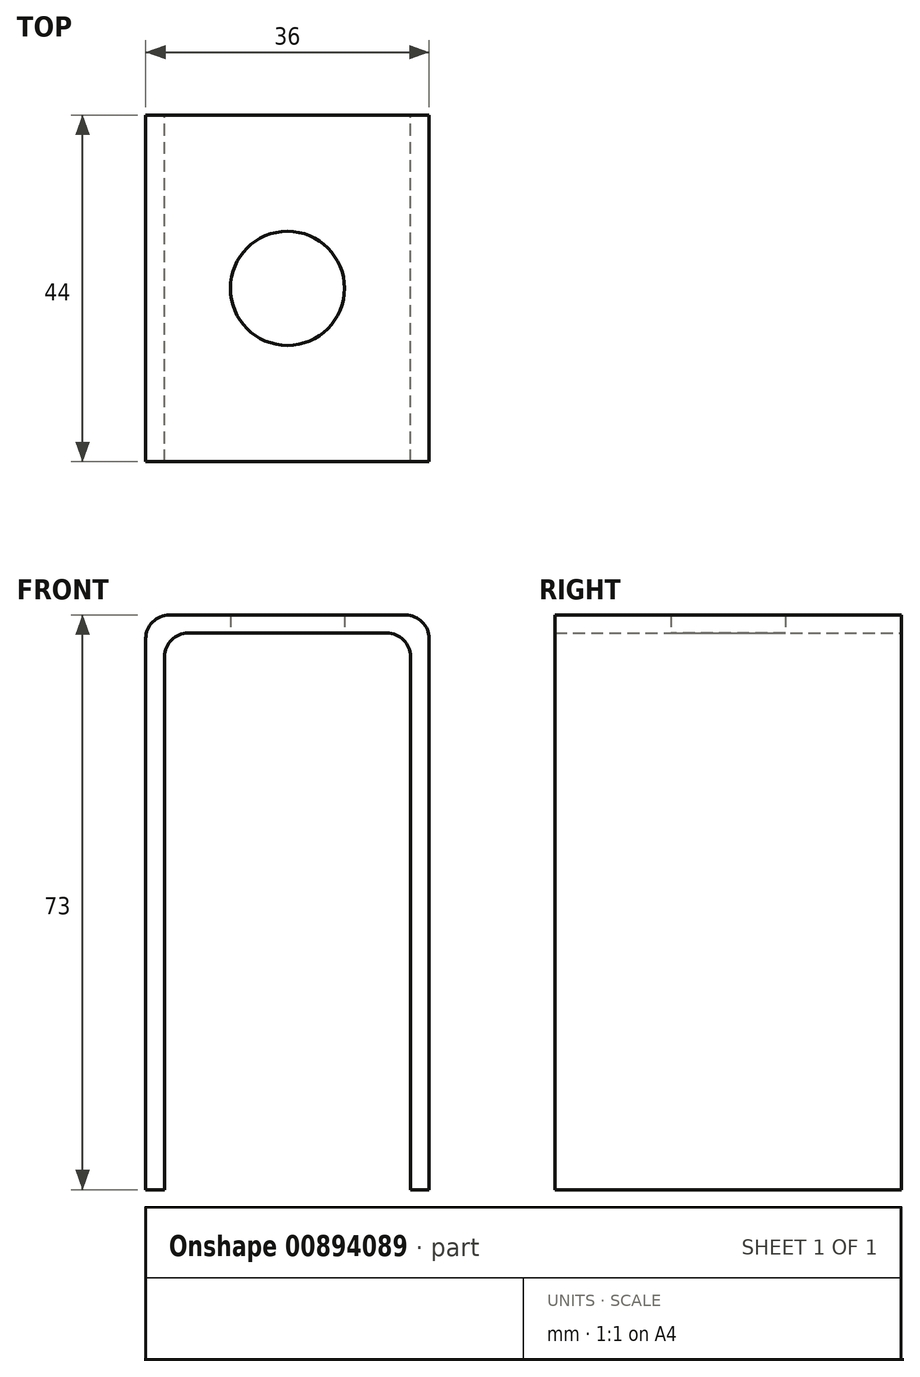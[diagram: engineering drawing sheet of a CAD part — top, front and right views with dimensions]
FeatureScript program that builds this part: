
annotation { "Feature Type Name" : "Feature", "Feature Type Description" : "" }
export const myFeature = defineFeature(function(context is Context, id is Id, definition is map)
    precondition{}
    {
        {
            var Q0;
            Q0=qCreatedBy(makeId("Front.planeOp"),FACE);
            var sketch = newSketch(context, id + "F0", { "sketchPlane" : qUnion([Q0])});
            skLineSegment(sketch, "E0", {"start": v(-16.5, 46.1) * mm, "end": v(8.74, 46.1) * mm});
            skLineSegment(sketch, "E1", {"start": v(-19.5, -24.63) * mm, "end": v(-19.5, 43.1) * mm});
            skLineSegment(sketch, "E2", {"start": v(11.74, 43.1) * mm, "end": v(11.74, -24.63) * mm});
            skPoint(sketch, "E3.visualSharp", {"position": v(-19.5, 46.1) * mm});
            skArc(sketch, "E3.filletArc", {"start": v(-16.5, 46.1) * mm, "mid": v(-18.62, 45.21) * mm, "end": v(-19.5, 43.1) * mm});
            skPoint(sketch, "E4.visualSharp", {"position": v(11.74, 46.1) * mm});
            skArc(sketch, "E4.filletArc", {"start": v(11.74, 43.1) * mm, "mid": v(10.87, 45.21) * mm, "end": v(8.74, 46.1) * mm});
            skLineSegment(sketch, "E5", {"start": v(-18.88, 48.37) * mm, "end": v(11.12, 48.37) * mm});
            skLineSegment(sketch, "E6", {"start": v(-21.88, 45.37) * mm, "end": v(-21.88, -24.63) * mm});
            skLineSegment(sketch, "E7", {"start": v(-21.88, -24.63) * mm, "end": v(-19.5, -24.63) * mm});
            skLineSegment(sketch, "E8", {"start": v(14.12, 45.37) * mm, "end": v(14.12, -24.63) * mm});
            skLineSegment(sketch, "E9", {"start": v(14.12, -24.63) * mm, "end": v(11.74, -24.63) * mm});
            skPoint(sketch, "E10.visualSharp", {"position": v(-21.88, 48.37) * mm});
            skArc(sketch, "E10.filletArc", {"start": v(-18.88, 48.37) * mm, "mid": v(-21, 47.5) * mm, "end": v(-21.88, 45.37) * mm});
            skPoint(sketch, "E11.visualSharp", {"position": v(14.12, 48.37) * mm});
            skArc(sketch, "E11.filletArc", {"start": v(14.12, 45.37) * mm, "mid": v(13.25, 47.5) * mm, "end": v(11.12, 48.37) * mm});
            skSolve(sketch);
        }
        {
            var Q0;
            Q0 = qSketchRegion(id + "F0", true);
            extrude(context, id + "F1", {"entities" : qUnion([Q0]), "depth" : 44 * mm, "offsetDistance" : 25 * mm});
        }
        {
            var Q0;
            Q0=qCreatedBy(makeId("Top.planeOp"),FACE);
            var sketch = newSketch(context, id + "F2", { "sketchPlane" : qUnion([Q0])});
            skCircle(sketch, "E12", {"center": v(-3.88, -22) * mm, "radius": 7.25 * mm});
            skSolve(sketch);
        }
        {
            var Q0;
            Q0 = qSketchRegion(id + "F2", true);
            extrude(context, id + "F3", {"entities" : qUnion([Q0]), "operationType" : NewBodyOperationType.REMOVE, "endBound" : BoundingType.SYMMETRIC, "depth" : 163.2 * mm, "offsetDistance" : 25 * mm});
        }
    });
